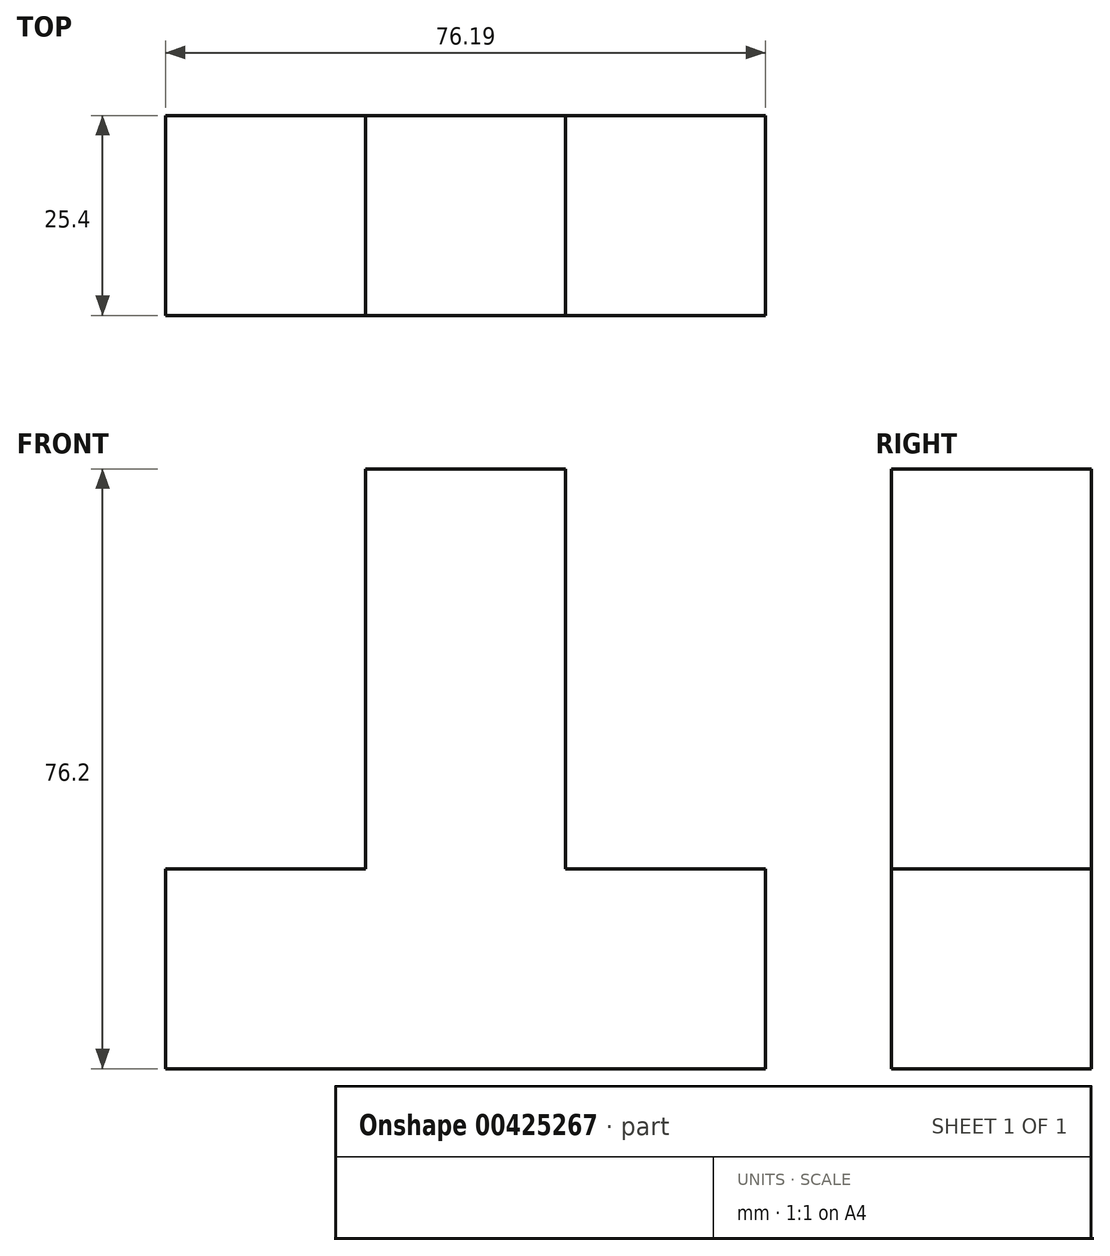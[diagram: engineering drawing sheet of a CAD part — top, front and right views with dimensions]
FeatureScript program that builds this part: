
annotation { "Feature Type Name" : "Feature", "Feature Type Description" : "" }
export const myFeature = defineFeature(function(context is Context, id is Id, definition is map)
    precondition{}
    {
        {
            var Q0;
            Q0=qCreatedBy(makeId("Front.planeOp"),FACE);
            var sketch = newSketch(context, id + "F0", { "sketchPlane" : qUnion([Q0])});
            skLineSegment(sketch, "E0", {"start": v(-48.12, -23.1) * mm, "end": v(28.07, -23.1) * mm});
            skLineSegment(sketch, "E1", {"start": v(28.07, -23.1) * mm, "end": v(28.07, 2.3) * mm});
            skLineSegment(sketch, "E2", {"start": v(28.07, 2.3) * mm, "end": v(2.67, 2.3) * mm});
            skLineSegment(sketch, "E3", {"start": v(2.67, 2.3) * mm, "end": v(2.67, 53.09) * mm});
            skLineSegment(sketch, "E4", {"start": v(2.67, 53.09) * mm, "end": v(-22.72, 53.09) * mm});
            skLineSegment(sketch, "E5", {"start": v(-22.72, 53.09) * mm, "end": v(-22.72, 2.3) * mm});
            skLineSegment(sketch, "E6", {"start": v(-22.72, 2.3) * mm, "end": v(-48.12, 2.3) * mm});
            skLineSegment(sketch, "E7", {"start": v(-48.12, 2.3) * mm, "end": v(-48.12, -23.1) * mm});
            skSolve(sketch);
        }
        {
            var Q0;
            Q0=makeQuery(id+"F0.imprint","IMPRINT",FACE,{"disambiguationData":[TD([[makeQuery(id+"F0.imprint","IMPRINT",EDGE,{"derivedFrom":sQuery(id+"F0.wireOp",EDGE,"E0")}),1.0]])]});
            extrude(context, id + "F1", {"entities" : qUnion([Q0]), "depth" : 25.4 * mm});
        }
    });
